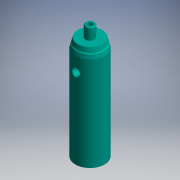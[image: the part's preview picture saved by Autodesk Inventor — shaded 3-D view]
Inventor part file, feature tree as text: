
AUTODESK INVENTOR PART (.ipt)
format: ipt  version: 2016 (Build 200138000, 138)  size: 215,552 bytes
history: native  units: mm (DEFAULTED — no unit token found)
features: other x2, extrude x1, sketch x1
ambient origin geometry x8: Origin, YZ Plane, XZ Plane, XY Plane, X Axis, Y Axis, Z Axis, Center Point
bodies: Solid1 (feature_tree), Solid2 (feature_tree)
feature tree (4):
  extrude  "Extrusion1"  [1 undecoded]
  sketch  "Sketch1"  dims[d0=5.2mm d1=0.0mm]
  other  "0331-001-1-solid1"
  other  "21110-001-1-solid1"
note: 1 required parameter value undecoded (feature->parameter linkage not recoverable at this tier; creation-order binding heuristic only, values carry confidence <= 0.55)
